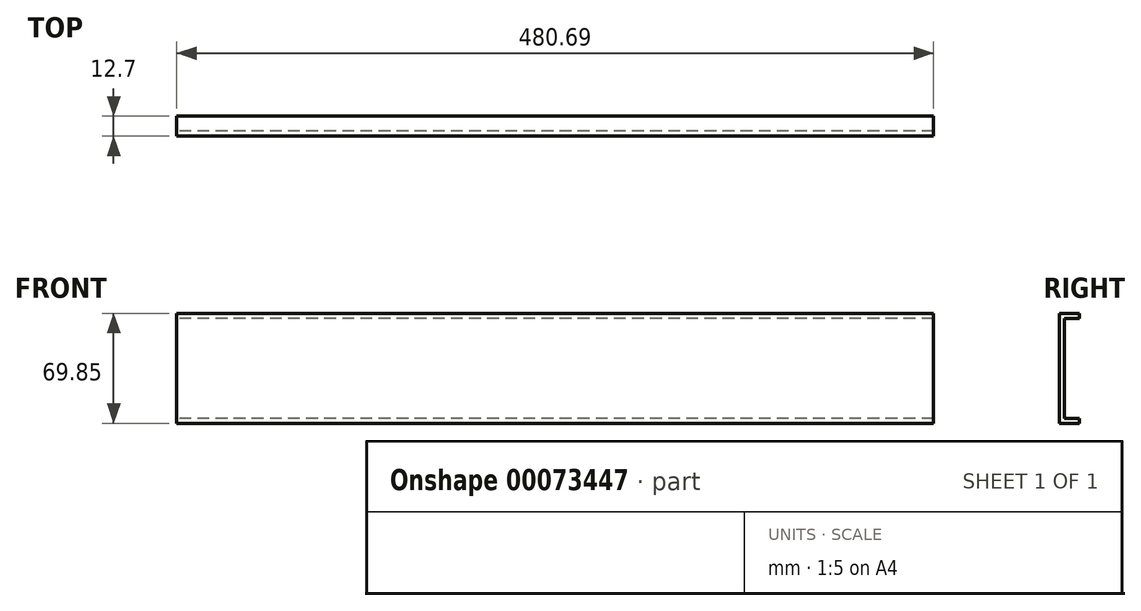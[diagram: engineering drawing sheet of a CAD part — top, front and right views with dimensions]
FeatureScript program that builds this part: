
annotation { "Feature Type Name" : "Feature", "Feature Type Description" : "" }
export const myFeature = defineFeature(function(context is Context, id is Id, definition is map)
    precondition{}
    {
        {
            var Q0;
            Q0=qCreatedBy(makeId("Right.planeOp"),FACE);
            var sketch = newSketch(context, id + "F0", { "sketchPlane" : qUnion([Q0])});
            skLineSegment(sketch, "E0", {"start": v(0, 36.12) * mm, "end": v(-12.7, 36.12) * mm});
            skLineSegment(sketch, "E1", {"start": v(-12.7, 36.12) * mm, "end": v(-12.7, -33.73) * mm});
            skLineSegment(sketch, "E2", {"start": v(-12.7, -33.73) * mm, "end": v(0, -33.73) * mm});
            skLineSegment(sketch, "E3", {"start": v(0, -33.73) * mm, "end": v(0, -30.56) * mm});
            skLineSegment(sketch, "E4", {"start": v(0, -30.56) * mm, "end": v(-9.52, -30.56) * mm});
            skLineSegment(sketch, "E5", {"start": v(-9.52, -30.56) * mm, "end": v(-9.53, 32.94) * mm});
            skLineSegment(sketch, "E6", {"start": v(-9.53, 32.94) * mm, "end": v(0, 32.94) * mm});
            skLineSegment(sketch, "E7", {"start": v(0, 32.94) * mm, "end": v(0, 36.12) * mm});
            skSolve(sketch);
        }
        {
            var Q0;
            Q0 = qSketchRegion(id + "F0", true);
            extrude(context, id + "F1", {"entities" : qUnion([Q0]), "depth" : 480.7 * mm});
        }
    });
